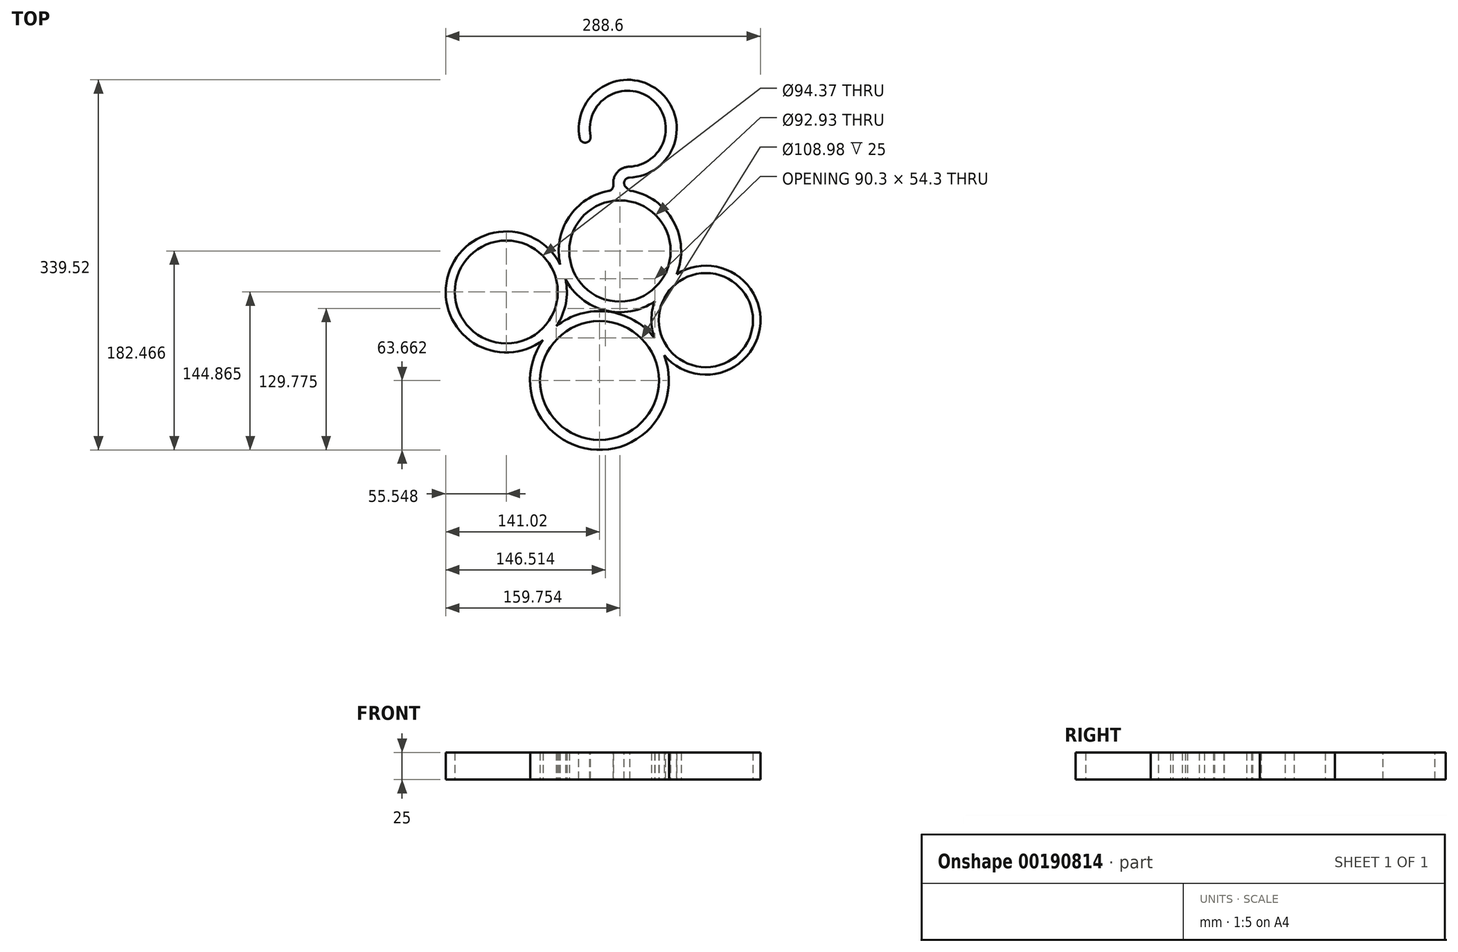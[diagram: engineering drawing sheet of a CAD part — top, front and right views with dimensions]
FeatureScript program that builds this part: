
annotation { "Feature Type Name" : "Feature", "Feature Type Description" : "" }
export const myFeature = defineFeature(function(context is Context, id is Id, definition is map)
    precondition{}
    {
        {
            var Q0;
            Q0=qCreatedBy(makeId("Top.planeOp"),FACE);
            var sketch = newSketch(context, id + "F0", { "sketchPlane" : qUnion([Q0])});
            skArc(sketch, "E0", {"start": v(-60.16, -113.14) * mm, "mid": v(27.57, -88.6) * mm, "end": v(-48.75, -38.86) * mm});
            skArc(sketch, "E1", {"start": v(-150.68, -43.11) * mm, "mid": v(-114.41, -72) * mm, "end": v(-68.78, -63.75) * mm});
            skArc(sketch, "E2", {"start": v(-159.09, -86.58) * mm, "mid": v(-150.37, -65.72) * mm, "end": v(-150.68, -43.11) * mm});
            skArc(sketch, "E3", {"start": v(-171.2, -99.32) * mm, "mid": v(-127.29, -199.55) * mm, "end": v(-60.16, -113.14) * mm});
            skCircle(sketch, "E4", {"center": v(-204.9, -55.18) * mm, "radius": 47.18 * mm});
            skCircle(sketch, "E5", {"center": v(-100.7, -17.57) * mm, "radius": 46.47 * mm});
            skCircle(sketch, "E6", {"center": v(-119.43, -136.38) * mm, "radius": 54.5 * mm});
            skCircle(sketch, "E7", {"center": v(-21.85, -81) * mm, "radius": 43.16 * mm});
            skArc(sketch, "E8.trimOffspring", {"start": v(-69.08, -97.41) * mm, "mid": v(-111.82, -73.17) * mm, "end": v(-159.09, -86.58) * mm});
            skArc(sketch, "E9.trimOffspring", {"start": v(-155.47, -29.84) * mm, "mid": v(-259.08, -42.92) * mm, "end": v(-171.2, -99.32) * mm});
            skArc(sketch, "E10.trimOffspring", {"start": v(-68.78, -63.75) * mm, "mid": v(-71.85, -80.56) * mm, "end": v(-69.08, -97.41) * mm});
            skArc(sketch, "E11.trimOffspring", {"start": v(-48.75, -38.86) * mm, "mid": v(-95.97, 38.36) * mm, "end": v(-155.47, -29.84) * mm});
            skSolve(sketch);
        }
        {
            var Q0;
            Q0=makeQuery(id+"F0.imprint","IMPRINT",FACE,{"disambiguationData":[TD([[makeQuery(id+"F0.imprint","IMPRINT",EDGE,{"derivedFrom":sQuery(id+"F0.wireOp",EDGE,"E0")}),1.0]])]});
            extrude(context, id + "F1", {"entities" : qUnion([Q0]), "depth" : 25 * mm});
        }
        {
            var Q0;
            Q0=makeQuery(id+"F1.opExtrude","CAP_FACE",FACE,{"disambiguationData":[OSD([sQuery(id+"F0.wireOp",EDGE,"E0"),sQuery(id+"F0.wireOp",EDGE,"E1"),sQuery(id+"F0.wireOp",EDGE,"E2"),sQuery(id+"F0.wireOp",EDGE,"E3"),sQuery(id+"F0.wireOp",EDGE,"E4"),sQuery(id+"F0.wireOp",EDGE,"E5"),sQuery(id+"F0.wireOp",EDGE,"E6"),sQuery(id+"F0.wireOp",EDGE,"E7"),sQuery(id+"F0.wireOp",EDGE,"E8.trimOffspring"),sQuery(id+"F0.wireOp",EDGE,"E9.trimOffspring"),sQuery(id+"F0.wireOp",EDGE,"E10.trimOffspring"),sQuery(id+"F0.wireOp",EDGE,"E11.trimOffspring")])],"isStart":false});
            var sketch = newSketch(context, id + "F2", { "sketchPlane" : qUnion([Q0])});
            skArc(sketch, "E12", {"start": v(-92.36, 59.77) * mm, "mid": v(-104.67, 52.6) * mm, "end": v(-105.42, 38.36) * mm});
            skArc(sketch, "E13", {"start": v(-92.36, 59.77) * mm, "mid": v(-71.83, 121.93) * mm, "end": v(-127.7, 87.83) * mm});
            skPoint(sketch, "E14", {"position": v(-95.97, 38.36) * mm});
            skArc(sketch, "E15.0", {"start": v(-92.03, 49.78) * mm, "mid": v(-65.61, 129.76) * mm, "end": v(-137.51, 85.88) * mm});
            skArc(sketch, "E15.1", {"start": v(-92.03, 49.78) * mm, "mid": v(-96.58, 46.46) * mm, "end": v(-95.16, 41.02) * mm});
            skLineSegment(sketch, "E16", {"start": v(-95.16, 41.02) * mm, "end": v(-91.47, 37.8) * mm});
            skArc(sketch, "E17.0", {"start": v(-91.47, 37.8) * mm, "mid": v(-98.43, 38.51) * mm, "end": v(-105.42, 38.36) * mm});
            skPoint(sketch, "E18.orphan", {"position": v(-155.47, -29.84) * mm});
            skPoint(sketch, "E19.orphan", {"position": v(-48.75, -38.86) * mm});
            skArc(sketch, "E20", {"start": v(-137.51, 85.88) * mm, "mid": v(-131.63, 81.95) * mm, "end": v(-127.7, 87.83) * mm});
            skSolve(sketch);
        }
        {
            var Q0;
            Q0 = qSketchRegion(id + "F2", true);
            extrude(context, id + "F3", {"entities" : qUnion([Q0]), "operationType" : NewBodyOperationType.ADD, "oppositeDirection" : true, "depth" : 25 * mm});
        }
        {
            var Q0;
            Q0=makeQuery(id+"F3.opExtrude","SWEPT_EDGE",EDGE,{"disambiguationData":[OSD([sQuery(id+"F0.wireOp",EDGE,"E11.trimOffspring"),sQuery(id+"F2.wireOp",EDGE,"E12"),sQuery(id+"F2.wireOp",EDGE,"E17.0")])]});
            var Q1;
            Q1=makeQuery(id+"F3.opExtrude","SWEPT_EDGE",EDGE,{"disambiguationData":[OSD([sQuery(id+"F0.wireOp",EDGE,"E11.trimOffspring"),sQuery(id+"F2.wireOp",EDGE,"E16"),sQuery(id+"F2.wireOp",EDGE,"E17.0")])]});
            fillet(context, id + "F4", {"entities" : qUnion([Q0, Q1]), "radius" : 5 * mm, "tangentPropagation" : true, "allowEdgeOverflow" : false});
        }
    });
